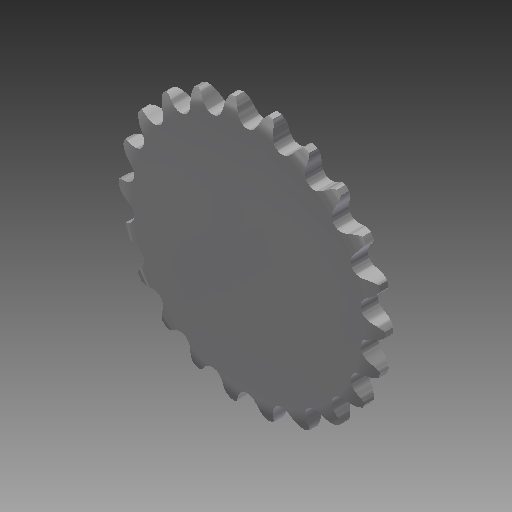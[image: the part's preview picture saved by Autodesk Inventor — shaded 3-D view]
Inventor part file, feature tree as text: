
AUTODESK INVENTOR PART (.ipt)
format: ipt  version: 2017 (Build 210142000, 142)  size: 616,448 bytes
history: native  units: mm
features: other x6, extrude x2, pattern_linear x1, pattern_circular x1
ambient origin geometry x8: Origin, YZ Plane, XZ Plane, XY Plane, X Axis, Y Axis, Z Axis, Center Point
bodies: Solid1 (feature_tree)
feature tree (10):
  other  "Theoretical Tooth Profile"
  other  "Tooth Profile"
  other  "Section Profile"
  other  "Shroud"
  other  "Strand"
  pattern_linear  "Strand Pattern"  Spacing1=44.619381mm  [1 undecoded]
  extrude  "Theoretical Tooth"  Depth=2.855993mm
  extrude  "Tooth"  Depth=1.697355mm
  pattern_circular  "Tooth Pattern"  [2 undecoded]
  other  "Timing Plane"
note: 3 required parameter values undecoded (feature->parameter linkage not recoverable at this tier; creation-order binding heuristic only, values carry confidence <= 0.55)
